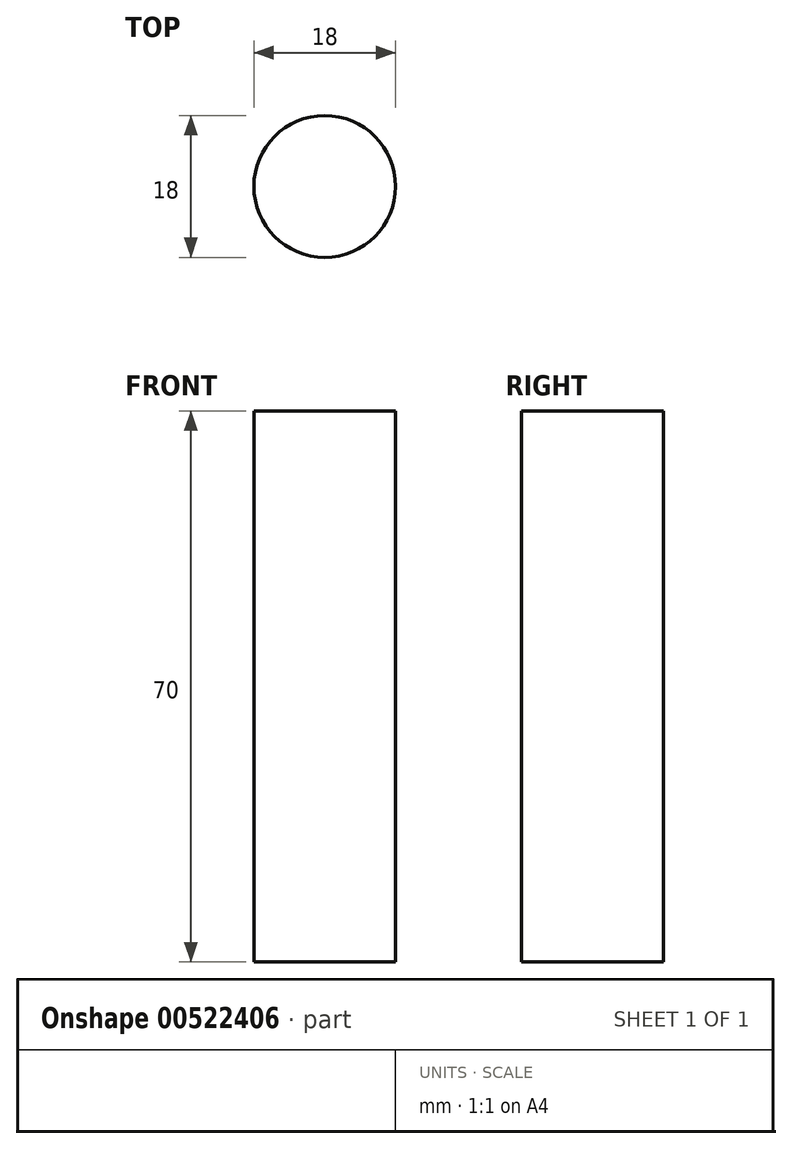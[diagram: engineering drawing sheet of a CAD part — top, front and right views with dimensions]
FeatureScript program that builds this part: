
annotation { "Feature Type Name" : "Feature", "Feature Type Description" : "" }
export const myFeature = defineFeature(function(context is Context, id is Id, definition is map)
    precondition{}
    {
        {
            var Q0;
            Q0=qCreatedBy(makeId("Top.planeOp"),FACE);
            var sketch = newSketch(context, id + "F0", { "sketchPlane" : qUnion([Q0])});
            skCircle(sketch, "E0", {"center": v(0, 0) * mm, "radius": 9 * mm});
            skSolve(sketch);
        }
        {
            var Q0;
            Q0=makeQuery(id+"F0.imprint","IMPRINT",FACE,{"disambiguationData":[TD([[makeQuery(id+"F0.imprint","IMPRINT",EDGE,{"derivedFrom":sQuery(id+"F0.wireOp",EDGE,"E0")}),1.0]])]});
            extrude(context, id + "F1", {"entities" : qUnion([Q0]), "depth" : 70 * mm, "offsetDistance" : 25 * mm});
        }
    });
